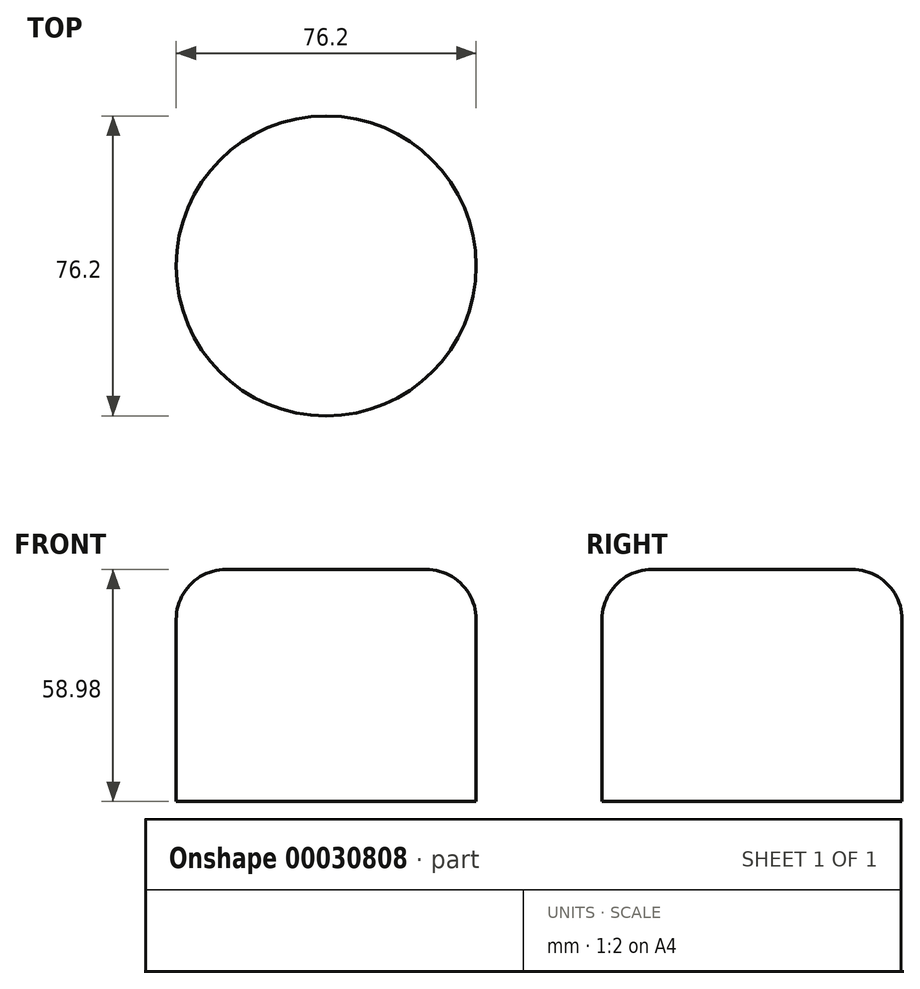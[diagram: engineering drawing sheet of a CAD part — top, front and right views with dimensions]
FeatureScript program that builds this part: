
annotation { "Feature Type Name" : "Feature", "Feature Type Description" : "" }
export const myFeature = defineFeature(function(context is Context, id is Id, definition is map)
    precondition{}
    {
        {
            var Q0;
            Q0=qCreatedBy(makeId("Top.planeOp"),FACE);
            var sketch = newSketch(context, id + "F0", { "sketchPlane" : qUnion([Q0])});
            skCircle(sketch, "E0", {"center": v(0, 0) * mm, "radius": 38.1 * mm});
            skSolve(sketch);
        }
        {
            var Q0;
            Q0 = qSketchRegion(id + "F0", true);
            extrude(context, id + "F1", {"entities" : qUnion([Q0]), "depth" : 58.98 * mm});
        }
        {
            var Q0;
            Q0=makeQuery(id+"F1.opExtrude","CAP_EDGE",EDGE,{"disambiguationData":[OSD([sQuery(id+"F0.wireOp",EDGE,"E0")])],"isStart":false});
            fillet(context, id + "F2", {"entities" : qUnion([Q0]), "radius" : 12.7 * mm, "tangentPropagation" : true, "allowEdgeOverflow" : false});
        }
    });
